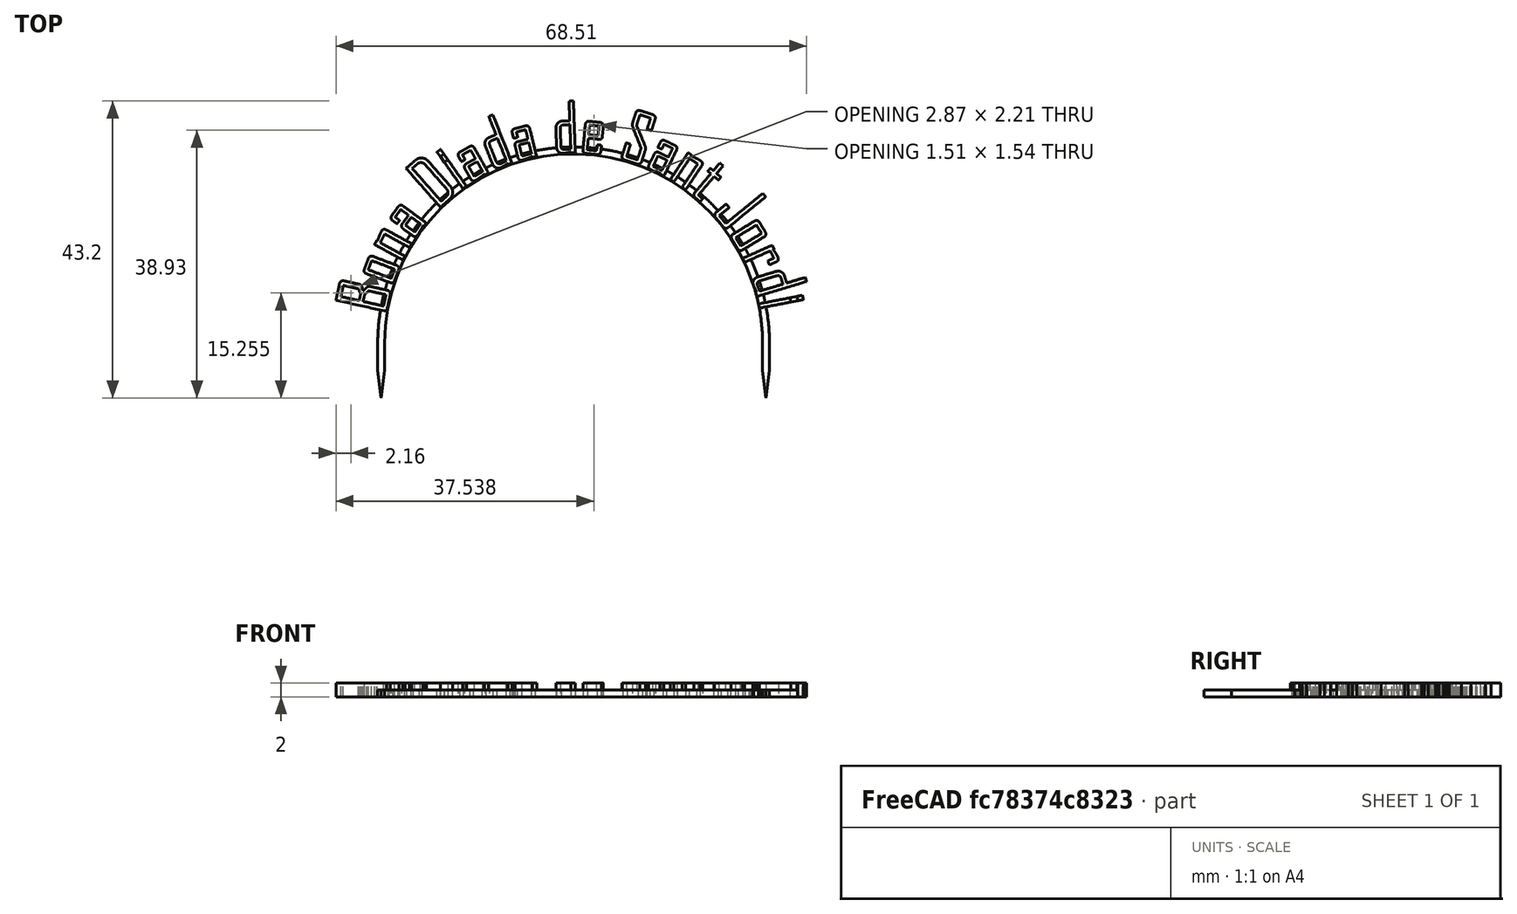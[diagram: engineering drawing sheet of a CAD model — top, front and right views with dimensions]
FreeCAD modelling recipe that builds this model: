
FCSTD DOCUMENT  (FreeCAD 0.20R29177 (Git))
Label: cake-topper-sant-jordi
License: All rights reserved
LicenseURL: http://en.wikipedia.org/wiki/All_rights_reserved
objects: Part::Feature×35, Sketcher::SketchObject×6, PartDesign::Pad×6, App::DocumentObjectGroup×5, App::TextDocument×1, Spreadsheet::Sheet×1, PartDesign::Plane×1, PartDesign::Body×1, Mesh::Feature×1
note: 55 computed .brp shape members not serialized (recipe doc carries the construction recipe); baked Part::Feature solids carry a one-line shape summary decoded from their .brp

FEATURE [App::TextDocument] Text_document  label="Text document"
FEATURE [Spreadsheet::Sheet] Spreadsheet
  cells = A1=Text height; B1=text_h; C1(dim_text_h)==2mm; A2=Text offset x; B2=text_x; C2(dim_text_x)==-105.3mm; A3=Text offset y; B3=text_y; C3(dim_text_y)==177.4mm; A4=Scaffold height; B4=scaffold_h; C4(dim_scaffold_h)==1mm; A5=Scaffold width; B5=scaffold_w; C5(dim_scaffold_w)==1mm; A6=Scaffold inner radius; B6=scaffold_ir; C6(dim_scaffold_ir)==27.5mm; A7=Scaffold outer radius; B7=scaffold_or; C7(dim_scaffold_or)==dim_scaffold_ir + dim_scaffold_w; A8=Tines length; B8=tine_l; C8(dim_tine_l)==4mm; A9=Tines shaft length; B9=tine_shaft_l; C9(dim_tine_shaft_l)==4mm
FEATURE [PartDesign::Plane] DatumPlane  label="BaseXYDatumPlane"
  Length = 81.3508
  MapMode = 5
  ResizeMode = 0
  Support = -> [XY_Plane]
  Width = 73.0447
FEATURE [Sketcher::SketchObject] Sketch001  label="ArcSketch"
  FullyConstrained = true
  MapMode = 5
  Support = -> [DatumPlane]
  expr: Constraints[15] = Spreadsheet.dim_scaffold_or
  expr: Constraints[37] = Spreadsheet.dim_tine_shaft_l
  expr: Constraints[38] = Spreadsheet.dim_tine_l
  expr: Constraints[59] = Spreadsheet.dim_scaffold_or
  expr: Constraints[6] = Spreadsheet.dim_scaffold_ir
  sketch-geometry (35):
    g0: ArcOfCircle CenterX=0 CenterY=0 CenterZ=0 NormalX=0 NormalY=0 NormalZ=1 AngleXU=0 Radius=27.5 StartAngle=0 EndAngle=3.14159
    g1: LineSegment StartX=-28.5 StartY=0 StartZ=0 EndX=-27.5 EndY=3.4e-15 EndZ=0
    g2: LineSegment StartX=27.5 StartY=0 StartZ=0 EndX=28.5 EndY=0 EndZ=0
    g3: ArcOfCircle CenterX=0 CenterY=0 CenterZ=0 NormalX=0 NormalY=0 NormalZ=1 AngleXU=0 Radius=28.5 StartAngle=0 EndAngle=0.185163
    g4: ArcOfCircle CenterX=0 CenterY=0 CenterZ=0 NormalX=0 NormalY=0 NormalZ=1 AngleXU=0 Radius=28.5 StartAngle=0.185163 EndAngle=0.207269
    g5: LineSegment StartX=27.89 StartY=5.86497 StartZ=0 EndX=33.2988 EndY=6.91633 EndZ=0
    g6: LineSegment StartX=28.0128 StartY=5.24706 StartZ=0 EndX=33.419 EndY=6.2979 EndZ=0
    g7: LineSegment StartX=33.2988 StartY=6.91633 StartZ=0 EndX=33.419 EndY=6.2979 EndZ=0
    g8: LineSegment StartX=-28.5 StartY=0 StartZ=0 EndX=-28.5 EndY=-4 EndZ=0
    g9: LineSegment StartX=-27.5 StartY=3.4e-15 StartZ=0 EndX=-27.5 EndY=-4 EndZ=0
    g10: LineSegment StartX=-28.5 StartY=-4 StartZ=0 EndX=-28 EndY=-8 EndZ=0
    g11: LineSegment StartX=-27.5 StartY=-4 StartZ=0 EndX=-28 EndY=-8 EndZ=0
    g12: LineSegment StartX=-28.5 StartY=-4 StartZ=0 EndX=-28 EndY=-4 EndZ=0
    g13: LineSegment StartX=-28 StartY=-4 StartZ=0 EndX=-27.5 EndY=-4 EndZ=0
    g14: LineSegment StartX=-28 StartY=-4 StartZ=0 EndX=-28 EndY=-8 EndZ=0
    g15: LineSegment StartX=27.5 StartY=-4 StartZ=0 EndX=28 EndY=-4 EndZ=0
    g16: LineSegment StartX=28 StartY=-4 StartZ=0 EndX=28.5 EndY=-4 EndZ=0
    g17: LineSegment StartX=28 StartY=-4 StartZ=0 EndX=28 EndY=-8 EndZ=0
    g18: LineSegment StartX=27.5 StartY=0 StartZ=0 EndX=27.5 EndY=-4 EndZ=0
    g19: LineSegment StartX=28.5 StartY=0 StartZ=0 EndX=28.5 EndY=-4 EndZ=0
    g20: LineSegment StartX=27.5 StartY=-4 StartZ=0 EndX=28 EndY=-8 EndZ=0
    g21: LineSegment StartX=28.5 StartY=-4 StartZ=0 EndX=28 EndY=-8 EndZ=0
    g22: LineSegment StartX=28.5 StartY=0 StartZ=0 EndX=28.5 EndY=28.5 EndZ=0
    g23: LineSegment StartX=27.89 StartY=5.86497 StartZ=0 EndX=0 EndY=5.86497 EndZ=0
    g24: ArcOfCircle CenterX=0 CenterY=0 CenterZ=0 NormalX=0 NormalY=0 NormalZ=1 AngleXU=0 Radius=28.5 StartAngle=2.19288 EndAngle=3.14159
    g25: ArcOfCircle CenterX=0 CenterY=0 CenterZ=0 NormalX=0 NormalY=0 NormalZ=1 AngleXU=0 Radius=28.5 StartAngle=0.207269 EndAngle=2.17112
    g26: ArcOfCircle CenterX=0 CenterY=0 CenterZ=0 NormalX=0 NormalY=0 NormalZ=1 AngleXU=0 Radius=28.5 StartAngle=2.17112 EndAngle=2.19288
    g27: LineSegment StartX=-16.6078 StartY=23.161 StartZ=0 EndX=-19.8518 EndY=27.7734 EndZ=0
    g28: LineSegment StartX=-16.1 StartY=23.5168 StartZ=0 EndX=-19.3446 EndY=28.13 EndZ=0
    g29: LineSegment StartX=-19.8518 StartY=27.7734 StartZ=0 EndX=-19.3446 EndY=28.13 EndZ=0
    g30: LineSegment StartX=-16.1 StartY=23.5168 StartZ=0 EndX=0 EndY=23.5168 EndZ=0
    g31: LineSegment StartX=28.5 StartY=28.5 StartZ=0 EndX=0 EndY=28.5 EndZ=0
    g32: LineSegment StartX=0 StartY=28.5 StartZ=0 EndX=-28.5 EndY=28.5 EndZ=0
    g33: LineSegment StartX=-28.5 StartY=0 StartZ=0 EndX=-28.5 EndY=28.5 EndZ=0
    g34: LineSegment StartX=-19.8518 StartY=28.5 StartZ=0 EndX=-19.8518 EndY=27.7734 EndZ=0
  constraints (96):
    c: Coincident(g0,g-1)
    c: PointOnObject(g0,g-1)
    c: PointOnObject(g0,g-1)
    c: Coincident(g3,g0)
    c: PointOnObject(g24,g-1)
    c: PointOnObject(g3,g-1)
    c: Radius(g0) = 27.5
    c: Coincident(g1,g24)
    c: Coincident(g1,g0)
    c: Coincident(g2,g0)
    c: Coincident(g2,g3)
    c: Coincident(g4,g25)
    c: Coincident(g3,g25)
    c: Coincident(g3,g4)
    c: Coincident(g3,g4)
    c: Radius(g3) = 28.5
    c: Coincident(g5,g25)
    c: Coincident(g6,g3)
    c: Coincident(g7,g5)
    c: Parallel(g5,g6)
    c: Perpendicular(g7,g5)
    c: Coincident(g8,g24)
    c: Vertical(g8)
    c: Coincident(g9,g0)
    c: Vertical(g9)
    c: Coincident(g10,g8)
    c: Coincident(g11,g9)
    c: Coincident(g11,g10)
    c: Coincident(g12,g8)
    c: Horizontal(g12)
    c: Coincident(g13,g12)
    c: Coincident(g13,g9)
    c: Horizontal(g13)
    c: Coincident(g14,g12)
    c: Coincident(g14,g10)
    c: Equal(g13,g12)
    c: Vertical(g14)
    c: DistanceY(g9,g9) = 4
    c: DistanceY(g10,g9) = 4
    c: Horizontal(g15)
    c: Coincident(g16,g15)
    c: Horizontal(g16)
    c: Coincident(g17,g15)
    c: Vertical(g17)
    c: Coincident(g18,g0)
    c: Coincident(g18,g15)
    c: Vertical(g18)
    c: Coincident(g19,g3)
    c: Coincident(g19,g16)
    c: Vertical(g19)
    c: Coincident(g20,g18)
    c: Coincident(g20,g17)
    c: Coincident(g21,g19)
    c: Coincident(g21,g20)
    c: Equal(g18,g9)
    c: Equal(g17,g14)
    c: Equal(g16,g15)
    c: Coincident(g22,g3)
    c: Vertical(g22)
    c: DistanceY(g22,g22) = 28.5
    c: Coincident(g7,g6)
    c: Coincident(g23,g25)
    c: PointOnObject(g23,g-2)
    c: Horizontal(g23)
    c: DistanceX(g23,g23) = 27.89
    c: Distance(g5) = 5.51
    c: Distance(g7) = 0.63
    c: Angle(g5,g22) = 1.37881
    c: Coincident(g26,g24)
    c: Coincident(g25,g24)
    c: Coincident(g25,g26)
    c: Coincident(g25,g26)
    c: Coincident(g27,g24)
    c: Coincident(g28,g25)
    c: Coincident(g29,g27)
    c: Coincident(g29,g28)
    c: Perpendicular(g27,g29)
    c: Distance(g29) = 0.62
    c: Perpendicular(g28,g29)
    c: Coincident(g30,g25)
    c: PointOnObject(g30,g-2)
    c: Horizontal(g30)
    c: DistanceX(g30,g30) = 16.1
    c: Coincident(g31,g22)
    c: PointOnObject(g31,g-2)
    c: Horizontal(g31)
    c: Coincident(g32,g31)
    c: Horizontal(g32)
    c: Coincident(g33,g8)
    c: Coincident(g33,g32)
    c: Vertical(g33)
    c: PointOnObject(g34,g32)
    c: Coincident(g34,g27)
    c: Vertical(g34)
    c: Angle(g29,g34) = 0.957837
    c: Distance(g28) = 5.64
FEATURE [PartDesign::Pad] Pad  label="ArcPad"
  Direction = (0,0,1)
  Length = 1
  Length2 = 10
  Profile = -> Sketch001
  ReferenceAxis = -> Sketch001 [N_Axis]
  Type = 0
  expr: Length = Spreadsheet.dim_scaffold_h
FEATURE [Part::Feature] path30594
  shape: bbox 7.938 x 4.471 x 2e-07 mm, 0 faces, 0 solids (baked)
FEATURE [Part::Feature] path30594001
  shape: bbox 2.874 x 2.205 x 2e-07 mm, 0 faces, 0 solids (baked)
FEATURE [Part::Feature] path30594002
  shape: bbox 3.342 x 2.199 x 2e-07 mm, 0 faces, 0 solids (baked)
FEATURE [Part::Feature] path30596
  shape: bbox 5.207 x 4.043 x 2e-07 mm, 0 faces, 0 solids (baked)
FEATURE [Part::Feature] path30596001
  shape: bbox 3.834 x 2.58 x 2e-07 mm, 0 faces, 0 solids (baked)
FEATURE [Part::Feature] path30598
  shape: bbox 5.411 x 4.523 x 2e-07 mm, 0 faces, 0 solids (baked)
FEATURE [Part::Feature] path30600
  shape: bbox 5.218 x 4.721 x 2e-07 mm, 0 faces, 0 solids (baked)
FEATURE [Part::Feature] path30600001
  shape: bbox 2.185 x 2.154 x 2e-07 mm, 0 faces, 0 solids (baked)
FEATURE [App::DocumentObjectGroup] Group  label="BonaGroup"
  Group = -> [path30594,path30594001,path30594002,path30596,path30596001,path30598,path30600,path30600001]
FEATURE [Part::Feature] path30602
  shape: bbox 6.817 x 7.204 x 2e-07 mm, 0 faces, 0 solids (baked)
FEATURE [Part::Feature] path30602001
  shape: bbox 5.23 x 5.635 x 2e-07 mm, 0 faces, 0 solids (baked)
FEATURE [Part::Feature] path30604
  shape: bbox 0.9987 x 1.037 x 2e-07 mm, 0 faces, 0 solids (baked)
FEATURE [Part::Feature] path30604001
  shape: bbox 3.216 x 4.202 x 2e-07 mm, 0 faces, 0 solids (baked)
FEATURE [Part::Feature] path30606
  shape: bbox 4.484 x 5.216 x 2e-07 mm, 0 faces, 0 solids (baked)
FEATURE [Part::Feature] path30606001
  shape: bbox 2.063 x 2.174 x 2e-07 mm, 0 faces, 0 solids (baked)
FEATURE [Part::Feature] path30608
  shape: bbox 3.975 x 7.801 x 2e-07 mm, 0 faces, 0 solids (baked)
FEATURE [Part::Feature] path30608001
  shape: bbox 2.556 x 3.792 x 2e-07 mm, 0 faces, 0 solids (baked)
FEATURE [Part::Feature] path30610
  shape: bbox 3.643 x 5.16 x 2e-07 mm, 0 faces, 0 solids (baked)
FEATURE [Part::Feature] path30610001
  shape: bbox 1.79 x 1.984 x 2e-07 mm, 0 faces, 0 solids (baked)
FEATURE [App::DocumentObjectGroup] Group001  label="DiadaGroup"
  Group = -> [path30602,path30602001,path30604,path30604001,path30606,path30606001,path30608,path30608001,path30610,path30610001]
FEATURE [Part::Feature] path30612
  shape: bbox 2.841 x 7.652 x 2e-07 mm, 0 faces, 0 solids (baked)
FEATURE [Part::Feature] path30612001
  shape: bbox 1.547 x 3.643 x 2e-07 mm, 0 faces, 0 solids (baked)
FEATURE [Part::Feature] path30614
  shape: bbox 3.068 x 4.926 x 2e-07 mm, 0 faces, 0 solids (baked)
FEATURE [Part::Feature] path30614001
  shape: bbox 1.51 x 1.541 x 2e-07 mm, 0 faces, 0 solids (baked)
FEATURE [App::DocumentObjectGroup] Group002  label="deGroup"
  Group = -> [path30612,path30612001,path30614,path30614001]
FEATURE [Part::Feature] path30616
  shape: bbox 4.887 x 7.86 x 2e-07 mm, 0 faces, 0 solids (baked)
FEATURE [Part::Feature] path30618
  shape: bbox 4.288 x 5.276 x 2e-07 mm, 0 faces, 0 solids (baked)
FEATURE [Part::Feature] path30618001
  shape: bbox 2.025 x 2.118 x 2e-07 mm, 0 faces, 0 solids (baked)
FEATURE [Part::Feature] path30620
  shape: bbox 4.747 x 5.4 x 2e-07 mm, 0 faces, 0 solids (baked)
FEATURE [Part::Feature] path30622
  shape: bbox 4.334 x 5.639 x 2e-07 mm, 0 faces, 0 solids (baked)
FEATURE [App::DocumentObjectGroup] Group003  label="SantGroup"
  Group = -> [path30616,path30618,path30618001,path30620,path30622]
FEATURE [Part::Feature] path30624
  shape: bbox 7.442 x 5.096 x 2e-07 mm, 0 faces, 0 solids (baked)
FEATURE [Part::Feature] path30626
  shape: bbox 5.181 x 4.513 x 2e-07 mm, 0 faces, 0 solids (baked)
FEATURE [Part::Feature] path30626001
  shape: bbox 3.779 x 3.06 x 2e-07 mm, 0 faces, 0 solids (baked)
FEATURE [Part::Feature] path30628
  shape: bbox 5.231 x 2.871 x 2e-07 mm, 0 faces, 0 solids (baked)
FEATURE [Part::Feature] path30630
  shape: bbox 7.839 x 3.715 x 2e-07 mm, 0 faces, 0 solids (baked)
FEATURE [Part::Feature] path30630001
  shape: bbox 3.802 x 2.33 x 2e-07 mm, 0 faces, 0 solids (baked)
FEATURE [Part::Feature] path30632
  shape: bbox 0.9195 x 0.7936 x 2e-07 mm, 0 faces, 0 solids (baked)
FEATURE [Part::Feature] path30632001
  shape: bbox 4.727 x 1.514 x 2e-07 mm, 0 faces, 0 solids (baked)
FEATURE [App::DocumentObjectGroup] Group004  label="JordiGroup"
  Group = -> [path30624,path30626,path30626001,path30628,path30630,path30630001,path30632,path30632001]
FEATURE [Sketcher::SketchObject] Sketch  label="BonaSketch"
  FullyConstrained = false
  Placement = pos=(-105.3,177.4,0) rot=(0,0,1;0rad)
  expr: .Placement.Base.x = Spreadsheet.dim_text_x
  expr: .Placement.Base.y = Spreadsheet.dim_text_y
  sketch-geometry (68):
    g0: BSplineCurve PolesCount=3 KnotsCount=2 Degree=2 IsPeriodic=0
    g1: BSplineCurve PolesCount=3 KnotsCount=2 Degree=2 IsPeriodic=0
    g2: BSplineCurve PolesCount=2 KnotsCount=2 Degree=1 IsPeriodic=0
    g3: BSplineCurve PolesCount=2 KnotsCount=2 Degree=1 IsPeriodic=0
    g4: BSplineCurve PolesCount=2 KnotsCount=2 Degree=1 IsPeriodic=0
    g5: BSplineCurve PolesCount=3 KnotsCount=2 Degree=2 IsPeriodic=0
    g6: BSplineCurve PolesCount=3 KnotsCount=2 Degree=2 IsPeriodic=0
    g7: BSplineCurve PolesCount=2 KnotsCount=2 Degree=1 IsPeriodic=0
    g8: BSplineCurve PolesCount=3 KnotsCount=2 Degree=2 IsPeriodic=0
    g9: BSplineCurve PolesCount=3 KnotsCount=2 Degree=2 IsPeriodic=0
    g10: BSplineCurve PolesCount=2 KnotsCount=2 Degree=1 IsPeriodic=0
    g11: BSplineCurve PolesCount=3 KnotsCount=2 Degree=2 IsPeriodic=0
    g12: BSplineCurve PolesCount=2 KnotsCount=2 Degree=1 IsPeriodic=0
    g13: BSplineCurve PolesCount=2 KnotsCount=2 Degree=1 IsPeriodic=0
    g14: BSplineCurve PolesCount=2 KnotsCount=2 Degree=1 IsPeriodic=0
    g15: BSplineCurve PolesCount=2 KnotsCount=2 Degree=1 IsPeriodic=0
    g16: BSplineCurve PolesCount=2 KnotsCount=2 Degree=1 IsPeriodic=0
    g17: BSplineCurve PolesCount=2 KnotsCount=2 Degree=1 IsPeriodic=0
    g18: BSplineCurve PolesCount=2 KnotsCount=2 Degree=1 IsPeriodic=0
    g19: BSplineCurve PolesCount=2 KnotsCount=2 Degree=1 IsPeriodic=0
    g20: BSplineCurve PolesCount=2 KnotsCount=2 Degree=1 IsPeriodic=0
    g21: BSplineCurve PolesCount=2 KnotsCount=2 Degree=1 IsPeriodic=0
    g22: BSplineCurve PolesCount=2 KnotsCount=2 Degree=1 IsPeriodic=0
    g23: BSplineCurve PolesCount=3 KnotsCount=2 Degree=2 IsPeriodic=0
    g24: BSplineCurve PolesCount=2 KnotsCount=2 Degree=1 IsPeriodic=0
    g25: BSplineCurve PolesCount=3 KnotsCount=2 Degree=2 IsPeriodic=0
    g26: BSplineCurve PolesCount=2 KnotsCount=2 Degree=1 IsPeriodic=0
    g27: BSplineCurve PolesCount=3 KnotsCount=2 Degree=2 IsPeriodic=0
    g28: BSplineCurve PolesCount=2 KnotsCount=2 Degree=1 IsPeriodic=0
    g29: BSplineCurve PolesCount=3 KnotsCount=2 Degree=2 IsPeriodic=0
    g30: BSplineCurve PolesCount=2 KnotsCount=2 Degree=1 IsPeriodic=0
    g31: BSplineCurve PolesCount=2 KnotsCount=2 Degree=1 IsPeriodic=0
    g32: BSplineCurve PolesCount=2 KnotsCount=2 Degree=1 IsPeriodic=0
    g33: BSplineCurve PolesCount=2 KnotsCount=2 Degree=1 IsPeriodic=0
    g34: BSplineCurve PolesCount=2 KnotsCount=2 Degree=1 IsPeriodic=0
    g35: BSplineCurve PolesCount=2 KnotsCount=2 Degree=1 IsPeriodic=0
    g36: BSplineCurve PolesCount=2 KnotsCount=2 Degree=1 IsPeriodic=0
    g37: BSplineCurve PolesCount=2 KnotsCount=2 Degree=1 IsPeriodic=0
    g38: BSplineCurve PolesCount=2 KnotsCount=2 Degree=1 IsPeriodic=0
    g39: BSplineCurve PolesCount=2 KnotsCount=2 Degree=1 IsPeriodic=0
    g40: BSplineCurve PolesCount=2 KnotsCount=2 Degree=1 IsPeriodic=0
    g41: BSplineCurve PolesCount=2 KnotsCount=2 Degree=1 IsPeriodic=0
    g42: BSplineCurve PolesCount=2 KnotsCount=2 Degree=1 IsPeriodic=0
    g43: BSplineCurve PolesCount=3 KnotsCount=2 Degree=2 IsPeriodic=0
    g44: BSplineCurve PolesCount=3 KnotsCount=2 Degree=2 IsPeriodic=0
    g45: BSplineCurve PolesCount=3 KnotsCount=2 Degree=2 IsPeriodic=0
    g46: BSplineCurve PolesCount=2 KnotsCount=2 Degree=1 IsPeriodic=0
    g47: BSplineCurve PolesCount=2 KnotsCount=2 Degree=1 IsPeriodic=0
    g48: BSplineCurve PolesCount=2 KnotsCount=2 Degree=1 IsPeriodic=0
    g49: BSplineCurve PolesCount=3 KnotsCount=2 Degree=2 IsPeriodic=0
    g50: BSplineCurve PolesCount=3 KnotsCount=2 Degree=2 IsPeriodic=0
    g51: BSplineCurve PolesCount=3 KnotsCount=2 Degree=2 IsPeriodic=0
    g52: BSplineCurve PolesCount=2 KnotsCount=2 Degree=1 IsPeriodic=0
    g53: BSplineCurve PolesCount=3 KnotsCount=2 Degree=2 IsPeriodic=0
    g54: BSplineCurve PolesCount=2 KnotsCount=2 Degree=1 IsPeriodic=0
    g55: BSplineCurve PolesCount=2 KnotsCount=2 Degree=1 IsPeriodic=0
    g56: BSplineCurve PolesCount=2 KnotsCount=2 Degree=1 IsPeriodic=0
    g57: BSplineCurve PolesCount=2 KnotsCount=2 Degree=1 IsPeriodic=0
    g58: BSplineCurve PolesCount=2 KnotsCount=2 Degree=1 IsPeriodic=0
    g59: BSplineCurve PolesCount=2 KnotsCount=2 Degree=1 IsPeriodic=0
    g60: BSplineCurve PolesCount=3 KnotsCount=2 Degree=2 IsPeriodic=0
    g61: BSplineCurve PolesCount=2 KnotsCount=2 Degree=1 IsPeriodic=0
    g62: BSplineCurve PolesCount=3 KnotsCount=2 Degree=2 IsPeriodic=0
    g63: BSplineCurve PolesCount=2 KnotsCount=2 Degree=1 IsPeriodic=0
    g64: BSplineCurve PolesCount=2 KnotsCount=2 Degree=1 IsPeriodic=0
    g65: BSplineCurve PolesCount=2 KnotsCount=2 Degree=1 IsPeriodic=0
    g66: BSplineCurve PolesCount=2 KnotsCount=2 Degree=1 IsPeriodic=0
    g67: BSplineCurve PolesCount=2 KnotsCount=2 Degree=1 IsPeriodic=0
  constraints (68):
    c: Coincident(g0,g1)
    c: Coincident(g1,g2)
    c: Coincident(g2,g3)
    c: Coincident(g3,g4)
    c: Coincident(g4,g5)
    c: Coincident(g5,g6)
    c: Coincident(g6,g7)
    c: Coincident(g7,g8)
    c: Coincident(g8,g9)
    c: Coincident(g9,g10)
    c: Coincident(g10,g11)
    c: Coincident(g11,g12)
    c: Coincident(g12,g0)
    c: Coincident(g13,g14)
    c: Coincident(g14,g15)
    c: Coincident(g15,g16)
    c: Coincident(g16,g17)
    c: Coincident(g17,g13)
    c: Coincident(g18,g19)
    c: Coincident(g19,g20)
    c: Coincident(g20,g21)
    c: Coincident(g21,g22)
    c: Coincident(g22,g18)
    c: Coincident(g23,g24)
    c: Coincident(g24,g25)
    c: Coincident(g25,g26)
    c: Coincident(g26,g27)
    c: Coincident(g27,g28)
    c: Coincident(g28,g29)
    c: Coincident(g29,g30)
    c: Coincident(g30,g23)
    c: Coincident(g31,g32)
    c: Coincident(g32,g33)
    c: Coincident(g33,g34)
    c: Coincident(g34,g31)
    c: Coincident(g35,g36)
    c: Coincident(g36,g37)
    c: Coincident(g37,g38)
    c: Coincident(g38,g39)
    c: Coincident(g39,g40)
    c: Coincident(g40,g41)
    c: Coincident(g41,g42)
    c: Coincident(g42,g43)
    c: Coincident(g43,g44)
    c: Coincident(g44,g45)
    c: Coincident(g45,g46)
    c: Coincident(g46,g35)
    c: Coincident(g47,g48)
    c: Coincident(g48,g49)
    c: Coincident(g49,g50)
    c: Coincident(g50,g51)
    c: Coincident(g51,g52)
    c: Coincident(g52,g53)
    c: Coincident(g53,g54)
    c: Coincident(g54,g55)
    c: Coincident(g55,g56)
    c: Coincident(g56,g57)
    c: Coincident(g57,g58)
    c: Coincident(g58,g59)
    c: Coincident(g59,g60)
    c: Coincident(g60,g61)
    c: Coincident(g61,g62)
    c: Coincident(g62,g63)
    c: Coincident(g63,g47)
    c: Coincident(g64,g65)
    c: Coincident(g65,g66)
    c: Coincident(g66,g67)
    c: Coincident(g67,g64)
FEATURE [Sketcher::SketchObject] Sketch002  label="DiadaSketch"
  FullyConstrained = false
  Placement = pos=(-105.3,177.4,0) rot=(0,0,1;0rad)
  expr: .Placement.Base.x = Spreadsheet.dim_text_x
  expr: .Placement.Base.y = Spreadsheet.dim_text_y
  sketch-geometry (84):
    g0: BSplineCurve PolesCount=3 KnotsCount=2 Degree=2 IsPeriodic=0
    g1: BSplineCurve PolesCount=3 KnotsCount=2 Degree=2 IsPeriodic=0
    g2: BSplineCurve PolesCount=2 KnotsCount=2 Degree=1 IsPeriodic=0
    g3: BSplineCurve PolesCount=2 KnotsCount=2 Degree=1 IsPeriodic=0
    g4: BSplineCurve PolesCount=2 KnotsCount=2 Degree=1 IsPeriodic=0
    g5: BSplineCurve PolesCount=3 KnotsCount=2 Degree=2 IsPeriodic=0
    g6: BSplineCurve PolesCount=3 KnotsCount=2 Degree=2 IsPeriodic=0
    g7: BSplineCurve PolesCount=2 KnotsCount=2 Degree=1 IsPeriodic=0
    g8: BSplineCurve PolesCount=2 KnotsCount=2 Degree=1 IsPeriodic=0
    g9: BSplineCurve PolesCount=3 KnotsCount=2 Degree=2 IsPeriodic=0
    g10: BSplineCurve PolesCount=3 KnotsCount=2 Degree=2 IsPeriodic=0
    g11: BSplineCurve PolesCount=2 KnotsCount=2 Degree=1 IsPeriodic=0
    g12: BSplineCurve PolesCount=2 KnotsCount=2 Degree=1 IsPeriodic=0
    g13: BSplineCurve PolesCount=2 KnotsCount=2 Degree=1 IsPeriodic=0
    g14: BSplineCurve PolesCount=3 KnotsCount=2 Degree=2 IsPeriodic=0
    g15: BSplineCurve PolesCount=3 KnotsCount=2 Degree=2 IsPeriodic=0
    g16: BSplineCurve PolesCount=2 KnotsCount=2 Degree=1 IsPeriodic=0
    g17: BSplineCurve PolesCount=2 KnotsCount=2 Degree=1 IsPeriodic=0
    g18: BSplineCurve PolesCount=2 KnotsCount=2 Degree=1 IsPeriodic=0
    g19: BSplineCurve PolesCount=2 KnotsCount=2 Degree=1 IsPeriodic=0
    g20: BSplineCurve PolesCount=2 KnotsCount=2 Degree=1 IsPeriodic=0
    g21: BSplineCurve PolesCount=2 KnotsCount=2 Degree=1 IsPeriodic=0
    g22: BSplineCurve PolesCount=2 KnotsCount=2 Degree=1 IsPeriodic=0
    g23: BSplineCurve PolesCount=2 KnotsCount=2 Degree=1 IsPeriodic=0
    g24: BSplineCurve PolesCount=2 KnotsCount=2 Degree=1 IsPeriodic=0
    g25: BSplineCurve PolesCount=2 KnotsCount=2 Degree=1 IsPeriodic=0
    g26: BSplineCurve PolesCount=3 KnotsCount=2 Degree=2 IsPeriodic=0
    g27: BSplineCurve PolesCount=3 KnotsCount=2 Degree=2 IsPeriodic=0
    g28: BSplineCurve PolesCount=3 KnotsCount=2 Degree=2 IsPeriodic=0
    g29: BSplineCurve PolesCount=2 KnotsCount=2 Degree=1 IsPeriodic=0
    g30: BSplineCurve PolesCount=3 KnotsCount=2 Degree=2 IsPeriodic=0
    g31: BSplineCurve PolesCount=2 KnotsCount=2 Degree=1 IsPeriodic=0
    g32: BSplineCurve PolesCount=2 KnotsCount=2 Degree=1 IsPeriodic=0
    g33: BSplineCurve PolesCount=2 KnotsCount=2 Degree=1 IsPeriodic=0
    g34: BSplineCurve PolesCount=2 KnotsCount=2 Degree=1 IsPeriodic=0
    g35: BSplineCurve PolesCount=2 KnotsCount=2 Degree=1 IsPeriodic=0
    g36: BSplineCurve PolesCount=2 KnotsCount=2 Degree=1 IsPeriodic=0
    g37: BSplineCurve PolesCount=3 KnotsCount=2 Degree=2 IsPeriodic=0
    g38: BSplineCurve PolesCount=2 KnotsCount=2 Degree=1 IsPeriodic=0
    g39: BSplineCurve PolesCount=3 KnotsCount=2 Degree=2 IsPeriodic=0
    g40: BSplineCurve PolesCount=2 KnotsCount=2 Degree=1 IsPeriodic=0
    g41: BSplineCurve PolesCount=2 KnotsCount=2 Degree=1 IsPeriodic=0
    g42: BSplineCurve PolesCount=2 KnotsCount=2 Degree=1 IsPeriodic=0
    g43: BSplineCurve PolesCount=2 KnotsCount=2 Degree=1 IsPeriodic=0
    g44: BSplineCurve PolesCount=2 KnotsCount=2 Degree=1 IsPeriodic=0
    g45: BSplineCurve PolesCount=2 KnotsCount=2 Degree=1 IsPeriodic=0
    g46: BSplineCurve PolesCount=2 KnotsCount=2 Degree=1 IsPeriodic=0
    g47: BSplineCurve PolesCount=3 KnotsCount=2 Degree=2 IsPeriodic=0
    g48: BSplineCurve PolesCount=3 KnotsCount=2 Degree=2 IsPeriodic=0
    g49: BSplineCurve PolesCount=3 KnotsCount=2 Degree=2 IsPeriodic=0
    g50: BSplineCurve PolesCount=2 KnotsCount=2 Degree=1 IsPeriodic=0
    g51: BSplineCurve PolesCount=3 KnotsCount=2 Degree=2 IsPeriodic=0
    g52: BSplineCurve PolesCount=3 KnotsCount=2 Degree=2 IsPeriodic=0
    g53: BSplineCurve PolesCount=2 KnotsCount=2 Degree=1 IsPeriodic=0
    g54: BSplineCurve PolesCount=2 KnotsCount=2 Degree=1 IsPeriodic=0
    g55: BSplineCurve PolesCount=2 KnotsCount=2 Degree=1 IsPeriodic=0
    g56: BSplineCurve PolesCount=2 KnotsCount=2 Degree=1 IsPeriodic=0
    g57: BSplineCurve PolesCount=2 KnotsCount=2 Degree=1 IsPeriodic=0
    g58: BSplineCurve PolesCount=2 KnotsCount=2 Degree=1 IsPeriodic=0
    g59: BSplineCurve PolesCount=3 KnotsCount=2 Degree=2 IsPeriodic=0
    g60: BSplineCurve PolesCount=2 KnotsCount=2 Degree=1 IsPeriodic=0
    g61: BSplineCurve PolesCount=3 KnotsCount=2 Degree=2 IsPeriodic=0
    g62: BSplineCurve PolesCount=3 KnotsCount=2 Degree=2 IsPeriodic=0
    g63: BSplineCurve PolesCount=2 KnotsCount=2 Degree=1 IsPeriodic=0
    g64: BSplineCurve PolesCount=2 KnotsCount=2 Degree=1 IsPeriodic=0
    g65: BSplineCurve PolesCount=3 KnotsCount=2 Degree=2 IsPeriodic=0
    g66: BSplineCurve PolesCount=3 KnotsCount=2 Degree=2 IsPeriodic=0
    g67: BSplineCurve PolesCount=3 KnotsCount=2 Degree=2 IsPeriodic=0
    g68: BSplineCurve PolesCount=2 KnotsCount=2 Degree=1 IsPeriodic=0
    g69: BSplineCurve PolesCount=3 KnotsCount=2 Degree=2 IsPeriodic=0
    g70: BSplineCurve PolesCount=2 KnotsCount=2 Degree=1 IsPeriodic=0
    g71: BSplineCurve PolesCount=2 KnotsCount=2 Degree=1 IsPeriodic=0
    g72: BSplineCurve PolesCount=2 KnotsCount=2 Degree=1 IsPeriodic=0
    g73: BSplineCurve PolesCount=2 KnotsCount=2 Degree=1 IsPeriodic=0
    g74: BSplineCurve PolesCount=2 KnotsCount=2 Degree=1 IsPeriodic=0
    g75: BSplineCurve PolesCount=2 KnotsCount=2 Degree=1 IsPeriodic=0
    g76: BSplineCurve PolesCount=3 KnotsCount=2 Degree=2 IsPeriodic=0
    g77: BSplineCurve PolesCount=2 KnotsCount=2 Degree=1 IsPeriodic=0
    g78: BSplineCurve PolesCount=3 KnotsCount=2 Degree=2 IsPeriodic=0
    g79: BSplineCurve PolesCount=2 KnotsCount=2 Degree=1 IsPeriodic=0
    g80: BSplineCurve PolesCount=2 KnotsCount=2 Degree=1 IsPeriodic=0
    g81: BSplineCurve PolesCount=2 KnotsCount=2 Degree=1 IsPeriodic=0
    g82: BSplineCurve PolesCount=2 KnotsCount=2 Degree=1 IsPeriodic=0
    g83: BSplineCurve PolesCount=2 KnotsCount=2 Degree=1 IsPeriodic=0
  constraints (84):
    c: Coincident(g0,g1)
    c: Coincident(g1,g2)
    c: Coincident(g2,g3)
    c: Coincident(g3,g4)
    c: Coincident(g4,g5)
    c: Coincident(g5,g6)
    c: Coincident(g6,g7)
    c: Coincident(g7,g0)
    c: Coincident(g8,g9)
    c: Coincident(g9,g10)
    c: Coincident(g10,g11)
    c: Coincident(g11,g12)
    c: Coincident(g12,g13)
    c: Coincident(g13,g14)
    c: Coincident(g14,g15)
    c: Coincident(g15,g8)
    c: Coincident(g16,g17)
    c: Coincident(g17,g18)
    c: Coincident(g18,g19)
    c: Coincident(g19,g16)
    c: Coincident(g20,g21)
    c: Coincident(g21,g22)
    c: Coincident(g22,g23)
    c: Coincident(g23,g20)
    c: Coincident(g24,g25)
    c: Coincident(g25,g26)
    c: Coincident(g26,g27)
    c: Coincident(g27,g28)
    c: Coincident(g28,g29)
    c: Coincident(g29,g30)
    c: Coincident(g30,g31)
    c: Coincident(g31,g32)
    c: Coincident(g32,g33)
    c: Coincident(g33,g34)
    c: Coincident(g34,g35)
    c: Coincident(g35,g36)
    c: Coincident(g36,g37)
    c: Coincident(g37,g38)
    c: Coincident(g38,g39)
    c: Coincident(g39,g40)
    c: Coincident(g40,g24)
    c: Coincident(g41,g42)
    c: Coincident(g42,g43)
    c: Coincident(g43,g44)
    c: Coincident(g44,g41)
    c: Coincident(g45,g46)
    c: Coincident(g46,g47)
    c: Coincident(g47,g48)
    c: Coincident(g48,g49)
    c: Coincident(g49,g50)
    c: Coincident(g50,g51)
    c: Coincident(g51,g52)
    c: Coincident(g52,g53)
    c: Coincident(g53,g54)
    c: Coincident(g54,g55)
    c: Coincident(g55,g56)
    c: Coincident(g56,g45)
    c: Coincident(g57,g58)
    c: Coincident(g58,g59)
    c: Coincident(g59,g60)
    c: Coincident(g60,g61)
    c: Coincident(g61,g62)
    c: Coincident(g62,g57)
    c: Coincident(g63,g64)
    c: Coincident(g64,g65)
    c: Coincident(g65,g66)
    c: Coincident(g66,g67)
    c: Coincident(g67,g68)
    c: Coincident(g68,g69)
    c: Coincident(g69,g70)
    c: Coincident(g70,g71)
    c: Coincident(g71,g72)
    c: Coincident(g72,g73)
    c: Coincident(g73,g74)
    c: Coincident(g74,g75)
    c: Coincident(g75,g76)
    c: Coincident(g76,g77)
    c: Coincident(g77,g78)
    c: Coincident(g78,g79)
    c: Coincident(g79,g63)
    c: Coincident(g80,g81)
    c: Coincident(g81,g82)
    c: Coincident(g82,g83)
    c: Coincident(g83,g80)
FEATURE [Sketcher::SketchObject] Sketch003  label="deSketch"
  FullyConstrained = false
  Placement = pos=(-105.3,177.4,0) rot=(0,0,1;0rad)
  expr: .Placement.Base.x = Spreadsheet.dim_text_x
  expr: .Placement.Base.y = Spreadsheet.dim_text_y
  sketch-geometry (38):
    g0: BSplineCurve PolesCount=2 KnotsCount=2 Degree=1 IsPeriodic=0
    g1: BSplineCurve PolesCount=2 KnotsCount=2 Degree=1 IsPeriodic=0
    g2: BSplineCurve PolesCount=3 KnotsCount=2 Degree=2 IsPeriodic=0
    g3: BSplineCurve PolesCount=3 KnotsCount=2 Degree=2 IsPeriodic=0
    g4: BSplineCurve PolesCount=3 KnotsCount=2 Degree=2 IsPeriodic=0
    g5: BSplineCurve PolesCount=2 KnotsCount=2 Degree=1 IsPeriodic=0
    g6: BSplineCurve PolesCount=3 KnotsCount=2 Degree=2 IsPeriodic=0
    g7: BSplineCurve PolesCount=3 KnotsCount=2 Degree=2 IsPeriodic=0
    g8: BSplineCurve PolesCount=2 KnotsCount=2 Degree=1 IsPeriodic=0
    g9: BSplineCurve PolesCount=2 KnotsCount=2 Degree=1 IsPeriodic=0
    g10: BSplineCurve PolesCount=2 KnotsCount=2 Degree=1 IsPeriodic=0
    g11: BSplineCurve PolesCount=2 KnotsCount=2 Degree=1 IsPeriodic=0
    g12: BSplineCurve PolesCount=2 KnotsCount=2 Degree=1 IsPeriodic=0
    g13: BSplineCurve PolesCount=2 KnotsCount=2 Degree=1 IsPeriodic=0
    g14: BSplineCurve PolesCount=3 KnotsCount=2 Degree=2 IsPeriodic=0
    g15: BSplineCurve PolesCount=2 KnotsCount=2 Degree=1 IsPeriodic=0
    g16: BSplineCurve PolesCount=3 KnotsCount=2 Degree=2 IsPeriodic=0
    g17: BSplineCurve PolesCount=3 KnotsCount=2 Degree=2 IsPeriodic=0
    g18: BSplineCurve PolesCount=2 KnotsCount=2 Degree=1 IsPeriodic=0
    g19: BSplineCurve PolesCount=3 KnotsCount=2 Degree=2 IsPeriodic=0
    g20: BSplineCurve PolesCount=2 KnotsCount=2 Degree=1 IsPeriodic=0
    g21: BSplineCurve PolesCount=3 KnotsCount=2 Degree=2 IsPeriodic=0
    g22: BSplineCurve PolesCount=2 KnotsCount=2 Degree=1 IsPeriodic=0
    g23: BSplineCurve PolesCount=3 KnotsCount=2 Degree=2 IsPeriodic=0
    g24: BSplineCurve PolesCount=2 KnotsCount=2 Degree=1 IsPeriodic=0
    g25: BSplineCurve PolesCount=3 KnotsCount=2 Degree=2 IsPeriodic=0
    g26: BSplineCurve PolesCount=2 KnotsCount=2 Degree=1 IsPeriodic=0
    g27: BSplineCurve PolesCount=2 KnotsCount=2 Degree=1 IsPeriodic=0
    g28: BSplineCurve PolesCount=2 KnotsCount=2 Degree=1 IsPeriodic=0
    g29: BSplineCurve PolesCount=2 KnotsCount=2 Degree=1 IsPeriodic=0
    g30: BSplineCurve PolesCount=2 KnotsCount=2 Degree=1 IsPeriodic=0
    g31: BSplineCurve PolesCount=2 KnotsCount=2 Degree=1 IsPeriodic=0
    g32: BSplineCurve PolesCount=2 KnotsCount=2 Degree=1 IsPeriodic=0
    g33: BSplineCurve PolesCount=2 KnotsCount=2 Degree=1 IsPeriodic=0
    g34: BSplineCurve PolesCount=2 KnotsCount=2 Degree=1 IsPeriodic=0
    g35: BSplineCurve PolesCount=2 KnotsCount=2 Degree=1 IsPeriodic=0
    g36: BSplineCurve PolesCount=2 KnotsCount=2 Degree=1 IsPeriodic=0
    g37: BSplineCurve PolesCount=2 KnotsCount=2 Degree=1 IsPeriodic=0
  constraints (38):
    c: Coincident(g0,g1)
    c: Coincident(g1,g2)
    c: Coincident(g2,g3)
    c: Coincident(g3,g4)
    c: Coincident(g4,g5)
    c: Coincident(g5,g6)
    c: Coincident(g6,g7)
    c: Coincident(g7,g8)
    c: Coincident(g8,g9)
    c: Coincident(g9,g10)
    c: Coincident(g10,g11)
    c: Coincident(g11,g0)
    c: Coincident(g12,g13)
    c: Coincident(g13,g14)
    c: Coincident(g14,g15)
    c: Coincident(g15,g16)
    c: Coincident(g16,g17)
    c: Coincident(g17,g18)
    c: Coincident(g18,g12)
    c: Coincident(g19,g20)
    c: Coincident(g20,g21)
    c: Coincident(g21,g22)
    c: Coincident(g22,g23)
    c: Coincident(g23,g24)
    c: Coincident(g24,g25)
    c: Coincident(g25,g26)
    c: Coincident(g26,g27)
    c: Coincident(g27,g28)
    c: Coincident(g28,g29)
    c: Coincident(g29,g30)
    c: Coincident(g30,g31)
    c: Coincident(g31,g32)
    c: Coincident(g32,g33)
    c: Coincident(g33,g19)
    c: Coincident(g34,g35)
    c: Coincident(g35,g36)
    c: Coincident(g36,g37)
    c: Coincident(g37,g34)
FEATURE [Sketcher::SketchObject] Sketch004  label="SantSketch"
  FullyConstrained = false
  Placement = pos=(-105.3,177.4,0) rot=(0,0,1;0rad)
  expr: .Placement.Base.x = Spreadsheet.dim_text_x
  expr: .Placement.Base.y = Spreadsheet.dim_text_y
  sketch-geometry (74):
    g0: BSplineCurve PolesCount=3 KnotsCount=2 Degree=2 IsPeriodic=0
    g1: BSplineCurve PolesCount=3 KnotsCount=2 Degree=2 IsPeriodic=0
    g2: BSplineCurve PolesCount=2 KnotsCount=2 Degree=1 IsPeriodic=0
    g3: BSplineCurve PolesCount=3 KnotsCount=2 Degree=2 IsPeriodic=0
    g4: BSplineCurve PolesCount=3 KnotsCount=2 Degree=2 IsPeriodic=0
    g5: BSplineCurve PolesCount=2 KnotsCount=2 Degree=1 IsPeriodic=0
    g6: BSplineCurve PolesCount=2 KnotsCount=2 Degree=1 IsPeriodic=0
    g7: BSplineCurve PolesCount=2 KnotsCount=2 Degree=1 IsPeriodic=0
    g8: BSplineCurve PolesCount=2 KnotsCount=2 Degree=1 IsPeriodic=0
    g9: BSplineCurve PolesCount=2 KnotsCount=2 Degree=1 IsPeriodic=0
    g10: BSplineCurve PolesCount=2 KnotsCount=2 Degree=1 IsPeriodic=0
    g11: BSplineCurve PolesCount=3 KnotsCount=2 Degree=2 IsPeriodic=0
    g12: BSplineCurve PolesCount=2 KnotsCount=2 Degree=1 IsPeriodic=0
    g13: BSplineCurve PolesCount=3 KnotsCount=2 Degree=2 IsPeriodic=0
    g14: BSplineCurve PolesCount=3 KnotsCount=2 Degree=2 IsPeriodic=0
    g15: BSplineCurve PolesCount=2 KnotsCount=2 Degree=1 IsPeriodic=0
    g16: BSplineCurve PolesCount=3 KnotsCount=2 Degree=2 IsPeriodic=0
    g17: BSplineCurve PolesCount=3 KnotsCount=2 Degree=2 IsPeriodic=0
    g18: BSplineCurve PolesCount=2 KnotsCount=2 Degree=1 IsPeriodic=0
    g19: BSplineCurve PolesCount=2 KnotsCount=2 Degree=1 IsPeriodic=0
    g20: BSplineCurve PolesCount=2 KnotsCount=2 Degree=1 IsPeriodic=0
    g21: BSplineCurve PolesCount=2 KnotsCount=2 Degree=1 IsPeriodic=0
    g22: BSplineCurve PolesCount=2 KnotsCount=2 Degree=1 IsPeriodic=0
    g23: BSplineCurve PolesCount=2 KnotsCount=2 Degree=1 IsPeriodic=0
    g24: BSplineCurve PolesCount=3 KnotsCount=2 Degree=2 IsPeriodic=0
    g25: BSplineCurve PolesCount=2 KnotsCount=2 Degree=1 IsPeriodic=0
    g26: BSplineCurve PolesCount=2 KnotsCount=2 Degree=1 IsPeriodic=0
    g27: BSplineCurve PolesCount=2 KnotsCount=2 Degree=1 IsPeriodic=0
    g28: BSplineCurve PolesCount=3 KnotsCount=2 Degree=2 IsPeriodic=0
    g29: BSplineCurve PolesCount=3 KnotsCount=2 Degree=2 IsPeriodic=0
    g30: BSplineCurve PolesCount=3 KnotsCount=2 Degree=2 IsPeriodic=0
    g31: BSplineCurve PolesCount=2 KnotsCount=2 Degree=1 IsPeriodic=0
    g32: BSplineCurve PolesCount=3 KnotsCount=2 Degree=2 IsPeriodic=0
    g33: BSplineCurve PolesCount=2 KnotsCount=2 Degree=1 IsPeriodic=0
    g34: BSplineCurve PolesCount=2 KnotsCount=2 Degree=1 IsPeriodic=0
    g35: BSplineCurve PolesCount=2 KnotsCount=2 Degree=1 IsPeriodic=0
    g36: BSplineCurve PolesCount=2 KnotsCount=2 Degree=1 IsPeriodic=0
    g37: BSplineCurve PolesCount=2 KnotsCount=2 Degree=1 IsPeriodic=0
    g38: BSplineCurve PolesCount=2 KnotsCount=2 Degree=1 IsPeriodic=0
    g39: BSplineCurve PolesCount=3 KnotsCount=2 Degree=2 IsPeriodic=0
    g40: BSplineCurve PolesCount=2 KnotsCount=2 Degree=1 IsPeriodic=0
    g41: BSplineCurve PolesCount=3 KnotsCount=2 Degree=2 IsPeriodic=0
    g42: BSplineCurve PolesCount=2 KnotsCount=2 Degree=1 IsPeriodic=0
    g43: BSplineCurve PolesCount=2 KnotsCount=2 Degree=1 IsPeriodic=0
    g44: BSplineCurve PolesCount=2 KnotsCount=2 Degree=1 IsPeriodic=0
    g45: BSplineCurve PolesCount=2 KnotsCount=2 Degree=1 IsPeriodic=0
    g46: BSplineCurve PolesCount=2 KnotsCount=2 Degree=1 IsPeriodic=0
    g47: BSplineCurve PolesCount=2 KnotsCount=2 Degree=1 IsPeriodic=0
    g48: BSplineCurve PolesCount=2 KnotsCount=2 Degree=1 IsPeriodic=0
    g49: BSplineCurve PolesCount=2 KnotsCount=2 Degree=1 IsPeriodic=0
    g50: BSplineCurve PolesCount=2 KnotsCount=2 Degree=1 IsPeriodic=0
    g51: BSplineCurve PolesCount=2 KnotsCount=2 Degree=1 IsPeriodic=0
    g52: BSplineCurve PolesCount=2 KnotsCount=2 Degree=1 IsPeriodic=0
    g53: BSplineCurve PolesCount=2 KnotsCount=2 Degree=1 IsPeriodic=0
    g54: BSplineCurve PolesCount=2 KnotsCount=2 Degree=1 IsPeriodic=0
    g55: BSplineCurve PolesCount=3 KnotsCount=2 Degree=2 IsPeriodic=0
    g56: BSplineCurve PolesCount=3 KnotsCount=2 Degree=2 IsPeriodic=0
    g57: BSplineCurve PolesCount=3 KnotsCount=2 Degree=2 IsPeriodic=0
    g58: BSplineCurve PolesCount=2 KnotsCount=2 Degree=1 IsPeriodic=0
    g59: BSplineCurve PolesCount=2 KnotsCount=2 Degree=1 IsPeriodic=0
    g60: BSplineCurve PolesCount=3 KnotsCount=2 Degree=2 IsPeriodic=0
    g61: BSplineCurve PolesCount=2 KnotsCount=2 Degree=1 IsPeriodic=0
    g62: BSplineCurve PolesCount=2 KnotsCount=2 Degree=1 IsPeriodic=0
    g63: BSplineCurve PolesCount=2 KnotsCount=2 Degree=1 IsPeriodic=0
    g64: BSplineCurve PolesCount=2 KnotsCount=2 Degree=1 IsPeriodic=0
    g65: BSplineCurve PolesCount=2 KnotsCount=2 Degree=1 IsPeriodic=0
    g66: BSplineCurve PolesCount=2 KnotsCount=2 Degree=1 IsPeriodic=0
    g67: BSplineCurve PolesCount=2 KnotsCount=2 Degree=1 IsPeriodic=0
    g68: BSplineCurve PolesCount=2 KnotsCount=2 Degree=1 IsPeriodic=0
    g69: BSplineCurve PolesCount=2 KnotsCount=2 Degree=1 IsPeriodic=0
    g70: BSplineCurve PolesCount=2 KnotsCount=2 Degree=1 IsPeriodic=0
    g71: BSplineCurve PolesCount=2 KnotsCount=2 Degree=1 IsPeriodic=0
    g72: BSplineCurve PolesCount=2 KnotsCount=2 Degree=1 IsPeriodic=0
    g73: BSplineCurve PolesCount=2 KnotsCount=2 Degree=1 IsPeriodic=0
  constraints (74):
    c: Coincident(g0,g1)
    c: Coincident(g1,g2)
    c: Coincident(g2,g3)
    c: Coincident(g3,g4)
    c: Coincident(g4,g5)
    c: Coincident(g5,g6)
    c: Coincident(g6,g7)
    c: Coincident(g7,g8)
    c: Coincident(g8,g9)
    c: Coincident(g9,g10)
    c: Coincident(g10,g11)
    c: Coincident(g11,g12)
    c: Coincident(g12,g13)
    c: Coincident(g13,g14)
    c: Coincident(g14,g15)
    c: Coincident(g15,g16)
    c: Coincident(g16,g17)
    c: Coincident(g17,g18)
    c: Coincident(g18,g19)
    c: Coincident(g19,g20)
    c: Coincident(g20,g21)
    c: Coincident(g21,g22)
    c: Coincident(g22,g23)
    c: Coincident(g23,g24)
    c: Coincident(g24,g25)
    c: Coincident(g25,g0)
    c: Coincident(g26,g27)
    c: Coincident(g27,g28)
    c: Coincident(g28,g29)
    c: Coincident(g29,g30)
    c: Coincident(g30,g31)
    c: Coincident(g31,g32)
    c: Coincident(g32,g33)
    c: Coincident(g33,g34)
    c: Coincident(g34,g35)
    c: Coincident(g35,g36)
    c: Coincident(g36,g37)
    c: Coincident(g37,g38)
    c: Coincident(g38,g39)
    c: Coincident(g39,g40)
    c: Coincident(g40,g41)
    c: Coincident(g41,g42)
    c: Coincident(g42,g26)
    c: Coincident(g43,g44)
    c: Coincident(g44,g45)
    c: Coincident(g45,g46)
    c: Coincident(g46,g43)
    c: Coincident(g47,g48)
    c: Coincident(g48,g49)
    c: Coincident(g49,g50)
    c: Coincident(g50,g51)
    c: Coincident(g51,g52)
    c: Coincident(g52,g53)
    c: Coincident(g53,g54)
    c: Coincident(g54,g55)
    c: Coincident(g55,g56)
    c: Coincident(g56,g57)
    c: Coincident(g57,g58)
    c: Coincident(g58,g47)
    c: Coincident(g59,g60)
    c: Coincident(g60,g61)
    c: Coincident(g61,g62)
    c: Coincident(g62,g63)
    c: Coincident(g63,g64)
    c: Coincident(g64,g65)
    c: Coincident(g65,g66)
    c: Coincident(g66,g67)
    c: Coincident(g67,g68)
    c: Coincident(g68,g69)
    c: Coincident(g69,g70)
    c: Coincident(g70,g71)
    c: Coincident(g71,g72)
    c: Coincident(g72,g73)
    c: Coincident(g73,g59)
FEATURE [Sketcher::SketchObject] Sketch005  label="JordiSketch"
  FullyConstrained = false
  Placement = pos=(-105.3,177.4,0) rot=(0,0,1;0rad)
  expr: .Placement.Base.x = Spreadsheet.dim_text_x
  expr: .Placement.Base.y = Spreadsheet.dim_text_y
  sketch-geometry (62):
    g0: BSplineCurve PolesCount=3 KnotsCount=2 Degree=2 IsPeriodic=0
    g1: BSplineCurve PolesCount=3 KnotsCount=2 Degree=2 IsPeriodic=0
    g2: BSplineCurve PolesCount=2 KnotsCount=2 Degree=1 IsPeriodic=0
    g3: BSplineCurve PolesCount=3 KnotsCount=2 Degree=2 IsPeriodic=0
    g4: BSplineCurve PolesCount=3 KnotsCount=2 Degree=2 IsPeriodic=0
    g5: BSplineCurve PolesCount=2 KnotsCount=2 Degree=1 IsPeriodic=0
    g6: BSplineCurve PolesCount=2 KnotsCount=2 Degree=1 IsPeriodic=0
    g7: BSplineCurve PolesCount=2 KnotsCount=2 Degree=1 IsPeriodic=0
    g8: BSplineCurve PolesCount=2 KnotsCount=2 Degree=1 IsPeriodic=0
    g9: BSplineCurve PolesCount=2 KnotsCount=2 Degree=1 IsPeriodic=0
    g10: BSplineCurve PolesCount=2 KnotsCount=2 Degree=1 IsPeriodic=0
    g11: BSplineCurve PolesCount=2 KnotsCount=2 Degree=1 IsPeriodic=0
    g12: BSplineCurve PolesCount=3 KnotsCount=2 Degree=2 IsPeriodic=0
    g13: BSplineCurve PolesCount=2 KnotsCount=2 Degree=1 IsPeriodic=0
    g14: BSplineCurve PolesCount=3 KnotsCount=2 Degree=2 IsPeriodic=0
    g15: BSplineCurve PolesCount=2 KnotsCount=2 Degree=1 IsPeriodic=0
    g16: BSplineCurve PolesCount=3 KnotsCount=2 Degree=2 IsPeriodic=0
    g17: BSplineCurve PolesCount=2 KnotsCount=2 Degree=1 IsPeriodic=0
    g18: BSplineCurve PolesCount=3 KnotsCount=2 Degree=2 IsPeriodic=0
    g19: BSplineCurve PolesCount=2 KnotsCount=2 Degree=1 IsPeriodic=0
    g20: BSplineCurve PolesCount=2 KnotsCount=2 Degree=1 IsPeriodic=0
    g21: BSplineCurve PolesCount=2 KnotsCount=2 Degree=1 IsPeriodic=0
    g22: BSplineCurve PolesCount=2 KnotsCount=2 Degree=1 IsPeriodic=0
    g23: BSplineCurve PolesCount=2 KnotsCount=2 Degree=1 IsPeriodic=0
    g24: BSplineCurve PolesCount=2 KnotsCount=2 Degree=1 IsPeriodic=0
    g25: BSplineCurve PolesCount=2 KnotsCount=2 Degree=1 IsPeriodic=0
    g26: BSplineCurve PolesCount=2 KnotsCount=2 Degree=1 IsPeriodic=0
    g27: BSplineCurve PolesCount=2 KnotsCount=2 Degree=1 IsPeriodic=0
    g28: BSplineCurve PolesCount=2 KnotsCount=2 Degree=1 IsPeriodic=0
    g29: BSplineCurve PolesCount=2 KnotsCount=2 Degree=1 IsPeriodic=0
    g30: BSplineCurve PolesCount=2 KnotsCount=2 Degree=1 IsPeriodic=0
    g31: BSplineCurve PolesCount=2 KnotsCount=2 Degree=1 IsPeriodic=0
    g32: BSplineCurve PolesCount=3 KnotsCount=2 Degree=2 IsPeriodic=0
    g33: BSplineCurve PolesCount=3 KnotsCount=2 Degree=2 IsPeriodic=0
    g34: BSplineCurve PolesCount=3 KnotsCount=2 Degree=2 IsPeriodic=0
    g35: BSplineCurve PolesCount=2 KnotsCount=2 Degree=1 IsPeriodic=0
    g36: BSplineCurve PolesCount=2 KnotsCount=2 Degree=1 IsPeriodic=0
    g37: BSplineCurve PolesCount=2 KnotsCount=2 Degree=1 IsPeriodic=0
    g38: BSplineCurve PolesCount=3 KnotsCount=2 Degree=2 IsPeriodic=0
    g39: BSplineCurve PolesCount=3 KnotsCount=2 Degree=2 IsPeriodic=0
    g40: BSplineCurve PolesCount=3 KnotsCount=2 Degree=2 IsPeriodic=0
    g41: BSplineCurve PolesCount=2 KnotsCount=2 Degree=1 IsPeriodic=0
    g42: BSplineCurve PolesCount=3 KnotsCount=2 Degree=2 IsPeriodic=0
    g43: BSplineCurve PolesCount=3 KnotsCount=2 Degree=2 IsPeriodic=0
    g44: BSplineCurve PolesCount=2 KnotsCount=2 Degree=1 IsPeriodic=0
    g45: BSplineCurve PolesCount=2 KnotsCount=2 Degree=1 IsPeriodic=0
    g46: BSplineCurve PolesCount=2 KnotsCount=2 Degree=1 IsPeriodic=0
    g47: BSplineCurve PolesCount=2 KnotsCount=2 Degree=1 IsPeriodic=0
    g48: BSplineCurve PolesCount=2 KnotsCount=2 Degree=1 IsPeriodic=0
    g49: BSplineCurve PolesCount=2 KnotsCount=2 Degree=1 IsPeriodic=0
    g50: BSplineCurve PolesCount=3 KnotsCount=2 Degree=2 IsPeriodic=0
    g51: BSplineCurve PolesCount=2 KnotsCount=2 Degree=1 IsPeriodic=0
    g52: BSplineCurve PolesCount=3 KnotsCount=2 Degree=2 IsPeriodic=0
    g53: BSplineCurve PolesCount=3 KnotsCount=2 Degree=2 IsPeriodic=0
    g54: BSplineCurve PolesCount=2 KnotsCount=2 Degree=1 IsPeriodic=0
    g55: BSplineCurve PolesCount=2 KnotsCount=2 Degree=1 IsPeriodic=0
    g56: BSplineCurve PolesCount=2 KnotsCount=2 Degree=1 IsPeriodic=0
    g57: BSplineCurve PolesCount=2 KnotsCount=2 Degree=1 IsPeriodic=0
    g58: BSplineCurve PolesCount=2 KnotsCount=2 Degree=1 IsPeriodic=0
    g59: BSplineCurve PolesCount=2 KnotsCount=2 Degree=1 IsPeriodic=0
    g60: BSplineCurve PolesCount=2 KnotsCount=2 Degree=1 IsPeriodic=0
    g61: BSplineCurve PolesCount=2 KnotsCount=2 Degree=1 IsPeriodic=0
  constraints (62):
    c: Coincident(g0,g1)
    c: Coincident(g1,g2)
    c: Coincident(g2,g3)
    c: Coincident(g3,g4)
    c: Coincident(g4,g5)
    c: Coincident(g5,g6)
    c: Coincident(g6,g7)
    c: Coincident(g7,g8)
    c: Coincident(g8,g9)
    c: Coincident(g9,g10)
    c: Coincident(g10,g11)
    c: Coincident(g11,g0)
    c: Coincident(g12,g13)
    c: Coincident(g13,g14)
    c: Coincident(g14,g15)
    c: Coincident(g15,g16)
    c: Coincident(g16,g17)
    c: Coincident(g17,g18)
    c: Coincident(g18,g19)
    c: Coincident(g19,g12)
    c: Coincident(g20,g21)
    c: Coincident(g21,g22)
    c: Coincident(g22,g23)
    c: Coincident(g23,g20)
    c: Coincident(g24,g25)
    c: Coincident(g25,g26)
    c: Coincident(g26,g27)
    c: Coincident(g27,g28)
    c: Coincident(g28,g29)
    c: Coincident(g29,g30)
    c: Coincident(g30,g31)
    c: Coincident(g31,g32)
    c: Coincident(g32,g33)
    c: Coincident(g33,g34)
    c: Coincident(g34,g35)
    c: Coincident(g35,g24)
    c: Coincident(g36,g37)
    c: Coincident(g37,g38)
    c: Coincident(g38,g39)
    c: Coincident(g39,g40)
    c: Coincident(g40,g41)
    c: Coincident(g41,g42)
    c: Coincident(g42,g43)
    c: Coincident(g43,g44)
    c: Coincident(g44,g45)
    c: Coincident(g45,g46)
    c: Coincident(g46,g47)
    c: Coincident(g47,g36)
    c: Coincident(g48,g49)
    c: Coincident(g49,g50)
    c: Coincident(g50,g51)
    c: Coincident(g51,g52)
    c: Coincident(g52,g53)
    c: Coincident(g53,g48)
    c: Coincident(g54,g55)
    c: Coincident(g55,g56)
    c: Coincident(g56,g57)
    c: Coincident(g57,g54)
    c: Coincident(g58,g59)
    c: Coincident(g59,g60)
    c: Coincident(g60,g61)
    c: Coincident(g61,g58)
FEATURE [PartDesign::Pad] Pad001  label="BonaPad"
  BaseFeature = -> Pad
  Direction = (0,0,1)
  Length = 2
  Length2 = 10
  Profile = -> Sketch
  ReferenceAxis = -> Sketch [N_Axis]
  Type = 0
  expr: Length = Spreadsheet.dim_text_h
FEATURE [PartDesign::Pad] Pad002  label="DiadaPad"
  BaseFeature = -> Pad001
  Direction = (0,0,1)
  Length = 2
  Length2 = 10
  Profile = -> Sketch002
  ReferenceAxis = -> Sketch002 [N_Axis]
  Type = 0
  expr: Length = Spreadsheet.dim_text_h
FEATURE [PartDesign::Pad] Pad003  label="dePad"
  BaseFeature = -> Pad002
  Direction = (0,0,1)
  Length = 2
  Length2 = 10
  Profile = -> Sketch003
  ReferenceAxis = -> Sketch003 [N_Axis]
  Type = 0
  expr: Length = Spreadsheet.dim_text_h
FEATURE [PartDesign::Pad] Pad004  label="SantPad"
  BaseFeature = -> Pad003
  Direction = (0,0,1)
  Length = 2
  Length2 = 10
  Profile = -> Sketch004
  ReferenceAxis = -> Sketch004 [N_Axis]
  Type = 0
  expr: Length = Spreadsheet.dim_text_h
FEATURE [PartDesign::Pad] Pad005  label="JordiPad"
  BaseFeature = -> Pad004
  Direction = (0,0,1)
  Length = 2
  Length2 = 10
  Profile = -> Sketch005
  ReferenceAxis = -> Sketch005 [N_Axis]
  Type = 0
  expr: Length = Spreadsheet.dim_text_h
FEATURE [PartDesign::Body] Body
  Group = -> [DatumPlane,Sketch001,Pad,Sketch,Sketch002,Sketch003,Sketch004,Sketch005,Pad001,Pad002,Pad003,Pad004,Pad005]
  Origin = -> Origin
  Tip = -> Pad005
FEATURE [Mesh::Feature] Mesh  label="Body (Meshed)"
